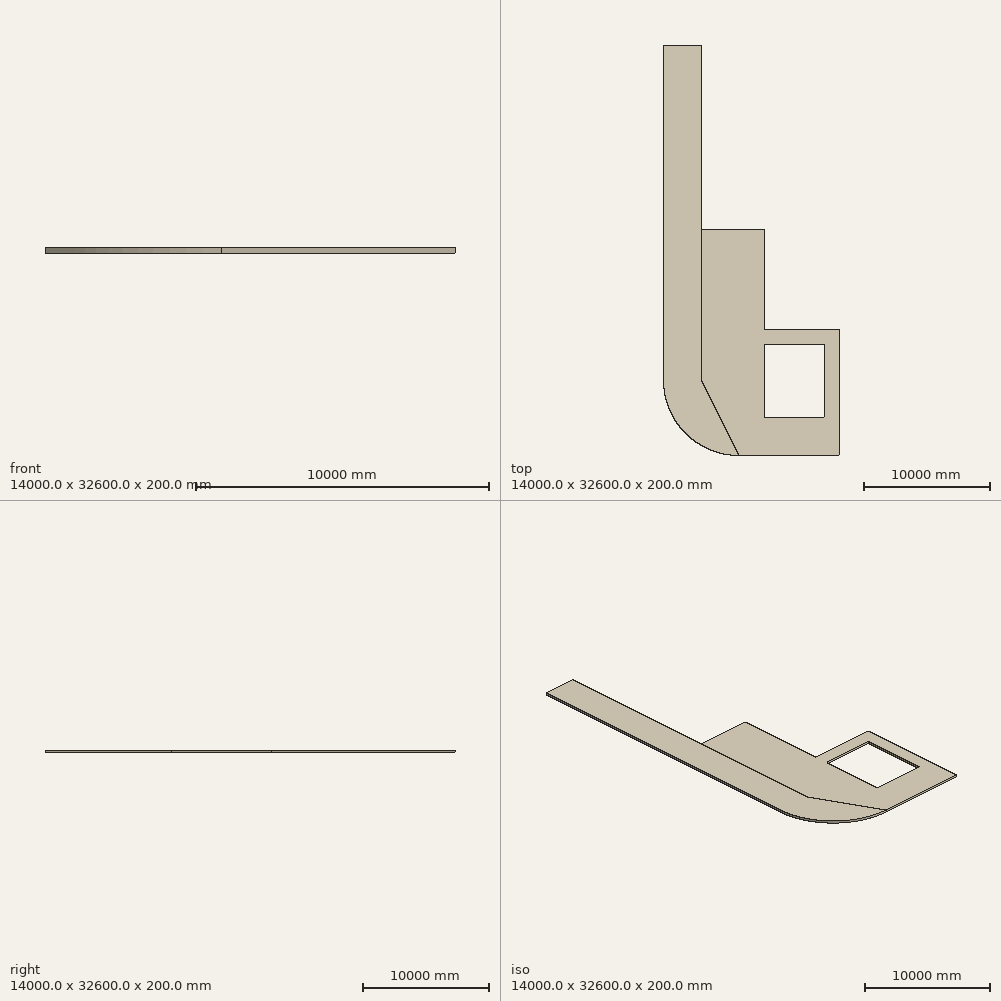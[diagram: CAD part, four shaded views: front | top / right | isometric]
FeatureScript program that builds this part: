
annotation { "Feature Type Name" : "Feature", "Feature Type Description" : "" }
export const myFeature = defineFeature(function(context is Context, id is Id, definition is map)
    precondition{}
    {
        {
            var Q0;
            Q0=qCreatedBy(makeId("Top.planeOp"),FACE);
            var sketch = newSketch(context, id + "F0", { "sketchPlane" : qUnion([Q0])});
            skLineSegment(sketch, "E0.bottom", {"start": v(-3000, 0) * mm, "end": v(0, 0) * mm});
            skLineSegment(sketch, "E0.top", {"start": v(-3000, -26600) * mm, "end": v(0, -26600) * mm});
            skLineSegment(sketch, "E0.left", {"start": v(-3000, 0) * mm, "end": v(-3000, -26600) * mm});
            skLineSegment(sketch, "E0.right", {"start": v(0, 0) * mm, "end": v(0, -26600) * mm});
            skLineSegment(sketch, "E1", {"start": v(0, -26600) * mm, "end": v(3000, -32600) * mm});
            skArc(sketch, "E2", {"start": v(-3000, -26600) * mm, "mid": v(-1242.64, -30842.64) * mm, "end": v(3000, -32600) * mm});
            skLineSegment(sketch, "E3", {"start": v(3000, -32600) * mm, "end": v(9515.66, -32600) * mm});
            skSolve(sketch);
        }
        {
            var Q0;
            Q0 = qSketchRegion(id + "F0", true);
            extrude(context, id + "F1", {"entities" : qUnion([Q0]), "depth" : 200 * mm, "offsetDistance" : 25 * mm});
        }
        {
            var Q0;
            Q0=qCreatedBy(makeId("Top.planeOp"),FACE);
            var sketch = newSketch(context, id + "F2", { "sketchPlane" : qUnion([Q0])});
            skLineSegment(sketch, "E4.0.0", {"start": v(-3000, 0) * mm, "end": v(-3000, -26600) * mm});
            skArc(sketch, "E4.0.1", {"start": v(-3000, -26600) * mm, "mid": v(-1242.64, -30842.64) * mm, "end": v(3000, -32600) * mm});
            skLineSegment(sketch, "E4.0.2", {"start": v(3000, -32600) * mm, "end": v(0, -26600) * mm});
            skLineSegment(sketch, "E4.0.3", {"start": v(0, -26600) * mm, "end": v(0, 0) * mm});
            skLineSegment(sketch, "E4.0.4", {"start": v(0, 0) * mm, "end": v(-3000, 0) * mm});
            skLineSegment(sketch, "E5", {"start": v(3000, -32600) * mm, "end": v(11000, -32600) * mm});
            skLineSegment(sketch, "E6", {"start": v(11000, -32600) * mm, "end": v(11000, -22600) * mm});
            skLineSegment(sketch, "E7", {"start": v(11000, -22600) * mm, "end": v(5000, -22600) * mm});
            skLineSegment(sketch, "E8", {"start": v(5000, -22600) * mm, "end": v(5000, -14600) * mm});
            skLineSegment(sketch, "E9", {"start": v(5000, -14600) * mm, "end": v(0, -14600) * mm});
            skLineSegment(sketch, "E10", {"start": v(0, -14600) * mm, "end": v(0, -26600) * mm});
            skLineSegment(sketch, "E11.bottom", {"start": v(5000, -23800) * mm, "end": v(9800, -23800) * mm});
            skLineSegment(sketch, "E11.top", {"start": v(5000, -29600) * mm, "end": v(9800, -29600) * mm});
            skLineSegment(sketch, "E11.left", {"start": v(5000, -23800) * mm, "end": v(5000, -29600) * mm});
            skLineSegment(sketch, "E11.right", {"start": v(9800, -23800) * mm, "end": v(9800, -29600) * mm});
            skSolve(sketch);
        }
        {
            var Q0;
            Q0=makeQuery(id+"F2.imprint","IMPRINT",FACE,{"disambiguationData":[TD([[makeQuery(id+"F2.imprint","IMPRINT",EDGE,{"derivedFrom":sQuery(id+"F2.wireOp",EDGE,"E4.0.2")}),-1.0]])]});
            extrude(context, id + "F3", {"entities" : qUnion([Q0]), "depth" : 200 * mm, "offsetDistance" : 25 * mm});
        }
    });
